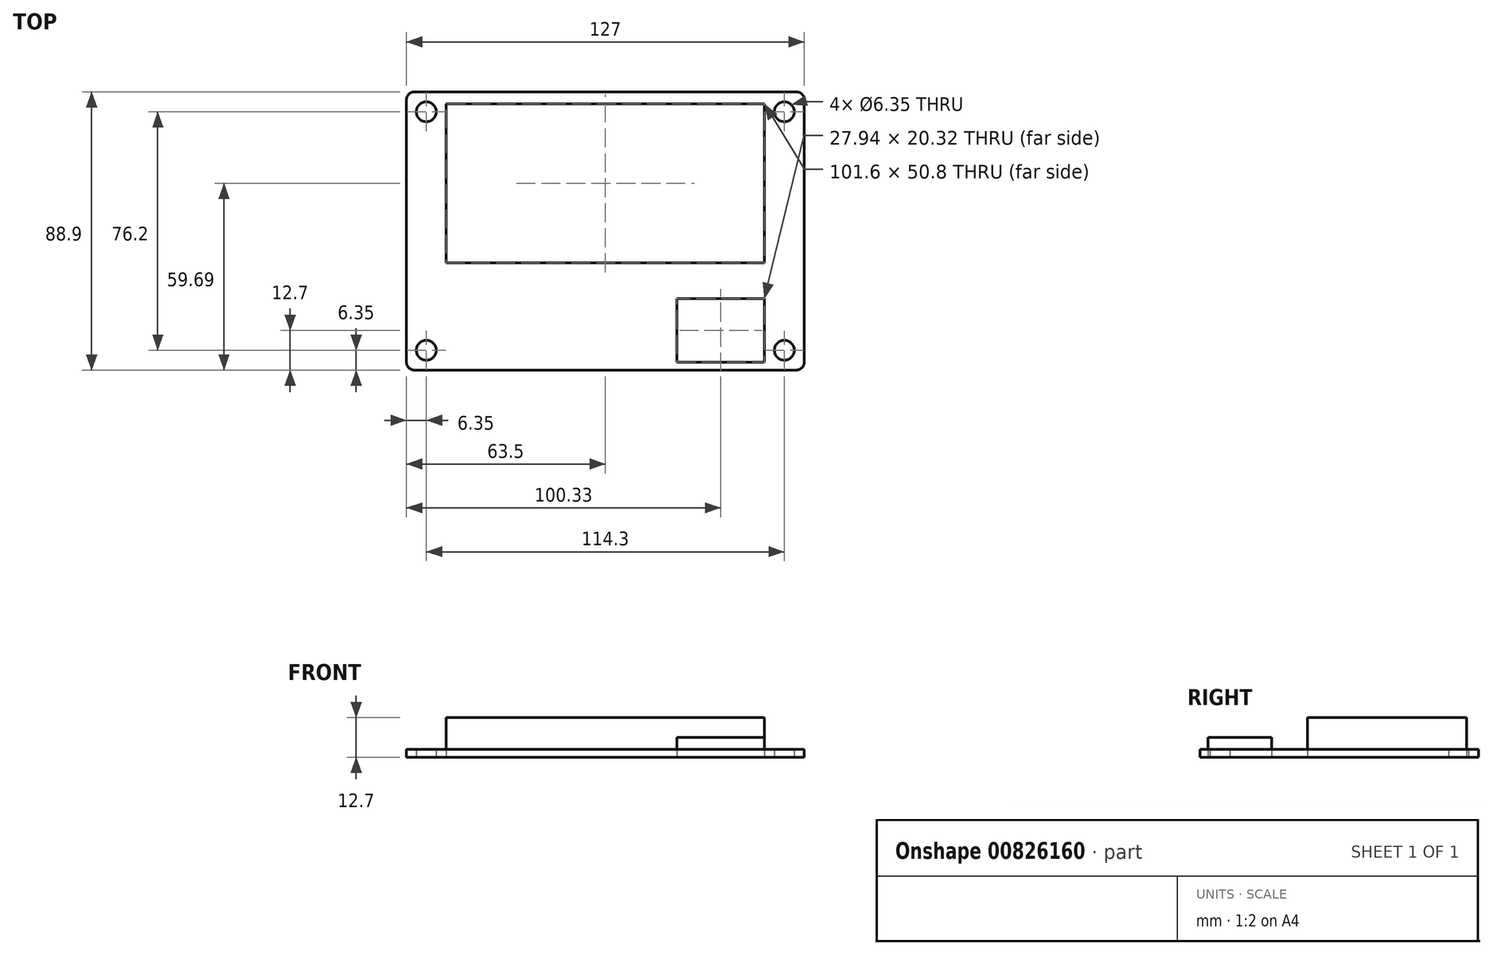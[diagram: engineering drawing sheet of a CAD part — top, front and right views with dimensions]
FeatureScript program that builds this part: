
annotation { "Feature Type Name" : "Feature", "Feature Type Description" : "" }
export const myFeature = defineFeature(function(context is Context, id is Id, definition is map)
    precondition{}
    {
        {
            var Q0;
            Q0=qCreatedBy(makeId("Top.planeOp"),FACE);
            var sketch = newSketch(context, id + "F0", { "sketchPlane" : qUnion([Q0])});
            skLineSegment(sketch, "E0.bottom", {"start": v(-60.96, 0) * mm, "end": v(60.96, 0) * mm});
            skLineSegment(sketch, "E0.top", {"start": v(-60.96, -88.9) * mm, "end": v(60.96, -88.9) * mm});
            skLineSegment(sketch, "E0.left", {"start": v(-63.5, -2.54) * mm, "end": v(-63.5, -86.36) * mm});
            skLineSegment(sketch, "E0.right", {"start": v(63.5, -2.54) * mm, "end": v(63.5, -86.36) * mm});
            skCircle(sketch, "E1", {"center": v(-57.15, -6.35) * mm, "radius": 3.18 * mm});
            skCircle(sketch, "E2", {"center": v(-57.15, -82.55) * mm, "radius": 3.18 * mm});
            skCircle(sketch, "E3", {"center": v(57.15, -82.55) * mm, "radius": 3.18 * mm});
            skCircle(sketch, "E4", {"center": v(57.15, -6.35) * mm, "radius": 3.18 * mm});
            skLineSegment(sketch, "E5.bottom", {"start": v(22.86, -66.04) * mm, "end": v(50.8, -66.04) * mm});
            skLineSegment(sketch, "E5.top", {"start": v(22.86, -86.36) * mm, "end": v(50.8, -86.36) * mm});
            skLineSegment(sketch, "E5.left", {"start": v(22.86, -66.04) * mm, "end": v(22.86, -86.36) * mm});
            skLineSegment(sketch, "E5.right", {"start": v(50.8, -66.04) * mm, "end": v(50.8, -86.36) * mm});
            skLineSegment(sketch, "E6.bottom", {"start": v(-50.8, -3.8) * mm, "end": v(50.8, -3.8) * mm});
            skLineSegment(sketch, "E6.top", {"start": v(-50.8, -54.6) * mm, "end": v(50.8, -54.6) * mm});
            skLineSegment(sketch, "E6.left", {"start": v(-50.8, -3.8) * mm, "end": v(-50.8, -54.6) * mm});
            skLineSegment(sketch, "E6.right", {"start": v(50.8, -3.8) * mm, "end": v(50.8, -54.6) * mm});
            skPoint(sketch, "E7.visualSharp", {"position": v(-63.5, 0) * mm});
            skArc(sketch, "E7.filletArc", {"start": v(-60.96, 0) * mm, "mid": v(-62.76, -0.74) * mm, "end": v(-63.5, -2.54) * mm});
            skPoint(sketch, "E8.visualSharp", {"position": v(-63.5, -88.9) * mm});
            skArc(sketch, "E8.filletArc", {"start": v(-63.5, -86.36) * mm, "mid": v(-62.76, -88.16) * mm, "end": v(-60.96, -88.9) * mm});
            skPoint(sketch, "E9.visualSharp", {"position": v(63.5, -88.9) * mm});
            skArc(sketch, "E9.filletArc", {"start": v(60.96, -88.9) * mm, "mid": v(62.76, -88.16) * mm, "end": v(63.5, -86.36) * mm});
            skPoint(sketch, "E10.visualSharp", {"position": v(63.5, 0) * mm});
            skArc(sketch, "E10.filletArc", {"start": v(63.5, -2.54) * mm, "mid": v(62.76, -0.74) * mm, "end": v(60.96, 0) * mm});
            skSolve(sketch);
        }
        {
            var Q0;
            Q0=makeQuery(id+"F0.imprint","IMPRINT",FACE,{"disambiguationData":[TD([[makeQuery(id+"F0.imprint","IMPRINT",EDGE,{"derivedFrom":sQuery(id+"F0.wireOp",EDGE,"E6.bottom")}),-1.0]])]});
            extrude(context, id + "F1", {"entities" : qUnion([Q0]), "depth" : 12.7 * mm, "offsetDistance" : 25.4 * mm});
        }
        {
            var Q0;
            Q0=makeQuery(id+"F0.imprint","IMPRINT",FACE,{"disambiguationData":[TD([[makeQuery(id+"F0.imprint","IMPRINT",EDGE,{"derivedFrom":sQuery(id+"F0.wireOp",EDGE,"E5.bottom")}),-1.0]])]});
            extrude(context, id + "F2", {"entities" : qUnion([Q0]), "depth" : 6.35 * mm, "offsetDistance" : 25.4 * mm});
        }
        {
            var Q0;
            Q0=makeQuery(id+"F0.imprint","IMPRINT",FACE,{"disambiguationData":[TD([[makeQuery(id+"F0.imprint","IMPRINT",EDGE,{"derivedFrom":sQuery(id+"F0.wireOp",EDGE,"E0.bottom")}),-1.0]])]});
            extrude(context, id + "F3", {"entities" : qUnion([Q0]), "depth" : 2.54 * mm, "offsetDistance" : 25.4 * mm});
        }
    });
